# Revit family: Basin-Vanity_Sink-American_Standard-Aspirations-180600X_Series
name_source: partatom
category: Plumbing Fixtures
units: mm (PartAtom-declared; Revit-internal decimal feet)

## family parameters
Always vertical = No
Cut with Voids When Loaded = Yes
OmniClass Number = 23.45.05.14.14
OmniClass Title = Sinks/Lavatories
Part Type = Normal
Room Calculation Point = No
Round Connector Dimension = Use Diameter
Shared = Yes
Work Plane-Based = No

## types (2) — shared parameters
ADA Compliant = Yes
ASME A112.19.2M for Vitreous China Fixtures = Yes
Assembly Code = D2010310
Basin Shape = Rectangular
Bowl Depth = 4 7/8"
CAN/CSA B45 series = Yes
CW Connection = Yes
CWFU = 1.5
Cold Water Connection Height = 10 3/4"
Cold Water Connection Width = 4"
Cold Water Diameter = 1/2"
Description = Aspirations™37-Inch by 22-Inch Vanity Top Sinks
Faucet hole HCW = 3 1/2"
Finish = Vitreous China-American Standard-020-White
HW Connection = Yes
HWFU = 1.5
Height = 6 1/2"
Hole Height = 4"
Hot Water Connection Diameter = 1/2"
Hot Water Connection Height = 10 3/4"
Hot Water Connection Width = 4"
Installation Type = Counter Top
Length = 37"
Manufacturer = American Standard
Material = Vitreous China-American Standard-020-White
Overflow Location = Front
Price = Prices may vary. Please consult Manufacturer Rep for most up-to-date price list.
URL = https://www.americanstandard-us.com
Vent Connection = No
WFU = 2
Waste Connection = Yes
Waste Connection Diameter = 1 1/4"
Width = 22"

## per-type parameters (varying)
| type | 1806001 Faucet holes - center hole only | 1806008 Faucet holes on 8" (203mm) centers | Default Elavation | Elevation Height | Hole Height adjust |
| 1806001.020 | Yes | No | 34" | 35" | 2" |
| 1806008.020 | No | Yes | 27" | 0" | 5" |

note: column(s) folded — value = type name in every type: Model

## geometry (parser evidence)
native form markers: Sweep x2
no freeform markers — native parametric forms only
